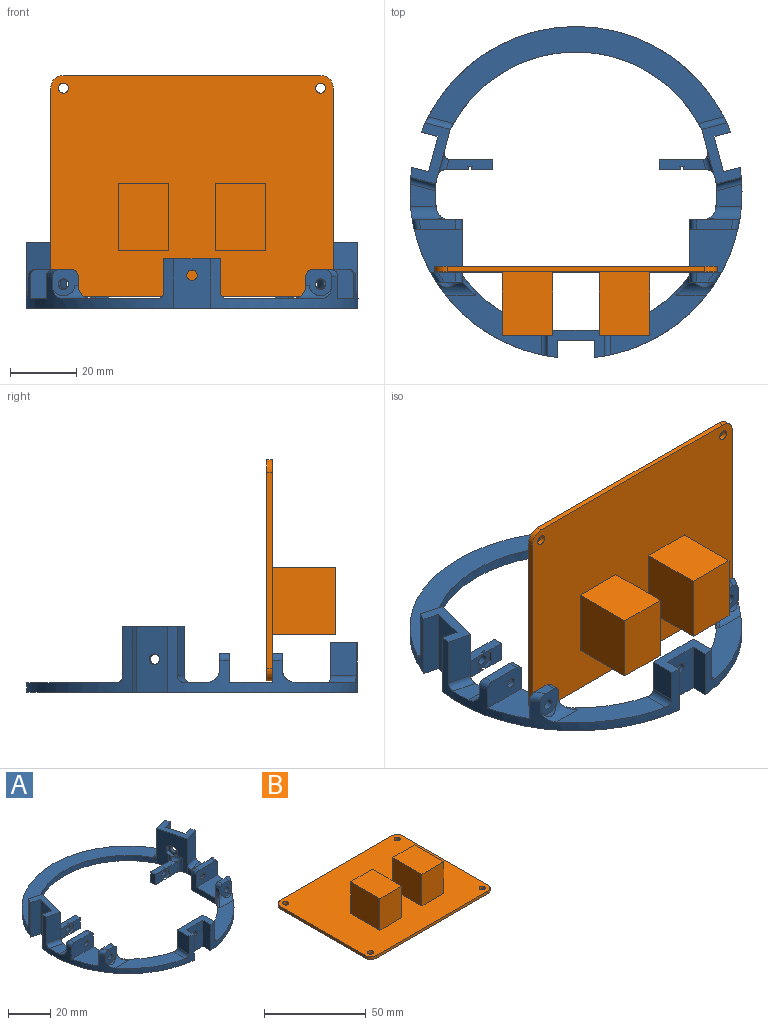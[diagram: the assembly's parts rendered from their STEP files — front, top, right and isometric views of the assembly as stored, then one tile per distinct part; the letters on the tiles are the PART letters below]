
ASSEMBLY  parts=2 mates=1
PART A: 151 faces, bbox 100.8x99.8x20.1 mm
  f0: plane 17x15mm, normal (0,1,0), area 227.6mm2, adj f1,f2,f28,f50,f52,f96,f97,f98
  f1: plane 10x7.77mm, normal (-1,0,0), area 77.7mm2, adj f0,f3,f128,f150
  f2: plane 10x7.77mm, normal (1,0,0), area 77.7mm2, adj f0,f4,f130,f150
  f3: cylinder r=50mm len=57.25mm, axis (0,0,-1), area 383.3mm2, adj f1,f5,f10,f27,f28,f29,f37,f40
  f4: cylinder r=50mm len=57.25mm, axis (0,0,-1), area 383.3mm2, adj f2,f7,f11,f23,f24,f28,f31,f32
  f5: plane 15x5.2mm, normal (1,0,0), area 77.9mm2, adj f3,f6,f28,f150
  f6: plane 15x11mm, normal (0,-1,0), area 157mm2, adj f5,f7,f22,f28,f150
  f7: plane 15x5.2mm, normal (-1,0,0), area 77.9mm2, adj f4,f6,f28,f150
  f8: cylinder r=1.6mm len=3.2mm, axis (0,1,0), area 30.2mm2, adj f54,f57
  f9: cylinder r=1.6mm len=3.2mm, axis (0,1,0), area 30.2mm2, adj f49,f61
  f10: cylinder r=4mm len=11.73mm, axis (1,0,0), area 33mm2, adj f3,f51,f61,f78,f149
  f11: cylinder r=4mm len=11.73mm, axis (1,0,0), area 33mm2, adj f4,f53,f54,f79,f148
  f12: plane 6.57x6mm, normal (0,-1,0), area 28.4mm2, adj f13,f28,f117,f135,f136,f137
  f13: plane 14.07x3.07mm, normal (0,0,1), area 40.2mm2, adj f12,f117,f118,f119,f125,f126,f137,f138
  f14: plane 7.18x6.07mm, normal (0,-1,0), area 32mm2, adj f16,f28,f123,f124,f141,f142,f143
  f15: plane 6.57x6mm, normal (0,-1,0), area 28.4mm2, adj f16,f28,f121,f144,f145,f146
  f16: plane 14.07x3.07mm, normal (0,0,1), area 40.2mm2, adj f14,f15,f120,f121,f122,f123,f143,f144
  f17: cylinder r=1.6mm len=3.2mm, axis (0,-1,0), area 20.1mm2, adj f120,f147
  f18: cylinder r=1.6mm len=3.2mm, axis (0,-1,0), area 20.1mm2, adj f118,f140
  f19: plane 20x16.42mm, normal (0.97,-0.26,0), area 257.2mm2, adj f26,f28,f29,f34,f36,f40,f103,f104
  f20: cylinder r=1.6mm len=3.48mm, axis (-0.97,-0.26,0), area 15.1mm2, adj f45,f116
  f21: cylinder r=1.6mm len=3.48mm, axis (0.97,-0.26,0), area 15.1mm2, adj f39,f109
  f22: cylinder r=1.6mm len=3.2mm, axis (0,1,0), area 15.1mm2, adj f6,f102
  f23: plane 15.18x11.9mm, normal (0,1,0), area 76.9mm2, adj f4,f24,f25,f28,f55,f60,f74,f75
  f24: cylinder r=4mm len=9.61mm, axis (-1,0,0), area 51.3mm2, adj f4,f23,f25,f30,f31,f89,f94
  f25: cylinder r=4mm len=4.92mm, axis (0,0,-1), area 23.3mm2, adj f23,f24,f28,f30,f89,f90
  f26: cylinder r=42.36mm len=7.17mm, axis (0,0,-1), area 22.4mm2, adj f19,f27,f28,f80,f81,f131
  f27: plane 7.85x6.71mm, normal (0,0,1), area 43.6mm2, adj f3,f26,f80,f131
  f28: plane 100x99.7mm, normal (0,0,-1), area 2314.5mm2, adj f0,f3,f4,f5,f6,f7,f12,f14
  f29: plane 15x7.51mm, normal (-0.26,-0.97,0), area 116.6mm2, adj f3,f19,f40,f131
  f30: cylinder r=42.36mm len=7.17mm, axis (0,0,-1), area 22.4mm2, adj f24,f25,f28,f31,f43,f129
  f31: plane 7.85x6.71mm, normal (0,0,1), area 43.6mm2, adj f4,f24,f30,f129
  f32: plane 15x7.51mm, normal (0.26,-0.97,0), area 116.6mm2, adj f4,f43,f46,f129
  f33: cylinder r=50mm len=93.16mm, axis (0,0,-1), area 464.4mm2, adj f28,f35,f36,f38,f40,f41,f42,f46
  f34: cylinder r=42.36mm len=75.77mm, axis (0,0,-1), area 283.1mm2, adj f19,f28,f35,f43,f132,f133
  f35: plane 89x29.24mm, normal (0,0,1), area 761.7mm2, adj f33,f34,f132,f133
  f36: plane 15x7.51mm, normal (0.26,0.97,0), area 116.6mm2, adj f19,f33,f40,f132
  f37: plane 20x5.02mm, normal (0.26,0.97,0), area 103.9mm2, adj f3,f28,f39,f40
  f38: plane 20x5.02mm, normal (-0.26,-0.97,0), area 103.9mm2, adj f28,f33,f39,f40
  f39: plane 20x10.63mm, normal (-0.97,0.26,0), area 212mm2, adj f21,f28,f37,f38,f40
  f40: plane 18.43x11.91mm, normal (0,0,1), area 81mm2, adj f3,f19,f29,f33,f36,f37,f38,f39
  f41: plane 15x7.51mm, normal (-0.26,0.97,0), area 116.6mm2, adj f33,f43,f46,f133
  f42: plane 20x5.02mm, normal (0.26,-0.97,0), area 103.9mm2, adj f28,f33,f45,f46
  f43: plane 20x16.42mm, normal (-0.97,-0.26,0), area 257.2mm2, adj f28,f30,f32,f34,f41,f46,f110,f111
  f44: plane 20x5.02mm, normal (-0.26,0.97,0), area 103.9mm2, adj f4,f28,f45,f46
  f45: plane 20x10.63mm, normal (0.97,0.26,0), area 212mm2, adj f20,f28,f42,f44,f46
  f46: plane 18.43x11.91mm, normal (0,0,1), area 81mm2, adj f4,f32,f33,f41,f42,f43,f44,f45
  f47: plane 18.8x9.76mm, normal (1,0,0), area 77.4mm2, adj f28,f48,f49,f61,f63,f64,f69,f70
  f48: plane 14.44x12.8mm, normal (0,0,1), area 158mm2, adj f3,f47,f49,f63
  f49: plane 9.57x8.76mm, normal (0,1,0), area 73.9mm2, adj f3,f9,f47,f48,f62,f68,f69
  f50: cylinder r=42.36mm len=25.39mm, axis (0,0,-1), area 96.7mm2, adj f0,f28,f51,f76,f78,f128
  f51: plane 28.73x19.27mm, normal (0,0,1), area 214.2mm2, adj f3,f10,f50,f78,f128
  f52: cylinder r=42.36mm len=25.39mm, axis (0,0,-1), area 96.7mm2, adj f0,f28,f53,f77,f79,f130
  f53: plane 28.73x19.27mm, normal (0,0,1), area 214.2mm2, adj f4,f11,f52,f79,f130
  f54: plane 7.95x7.79mm, normal (0,-1,0), area 44.2mm2, adj f4,f8,f11,f55,f58,f72,f73,f148
  f55: plane 18.8x9.76mm, normal (-1,0,0), area 77.4mm2, adj f23,f28,f54,f56,f57,f59,f72,f74
  f56: plane 14.44x12.8mm, normal (0,0,1), area 158mm2, adj f4,f55,f57,f59
  f57: plane 9.57x8.76mm, normal (0,1,0), area 73.9mm2, adj f4,f8,f55,f56,f58,f72,f73
  f58: plane 5.28x3mm, normal (0,0,1), area 13.1mm2, adj f54,f57,f72,f73
  f59: plane 14.44x8.76mm, normal (0,-1,0), area 116.6mm2, adj f4,f55,f56,f60,f67,f74,f75
  f60: plane 11x3mm, normal (0,0,1), area 32.1mm2, adj f23,f59,f74,f75
  f61: plane 7.95x7.79mm, normal (0,-1,0), area 44.1mm2, adj f3,f9,f10,f47,f62,f68,f69,f149
  f62: plane 5.28x3mm, normal (0,0,1), area 13.1mm2, adj f49,f61,f68,f69
  f63: plane 14.44x8.76mm, normal (0,-1,0), area 116.6mm2, adj f3,f47,f48,f65,f66,f70,f71
  f64: plane 15.18x11.9mm, normal (0,1,0), area 76.9mm2, adj f3,f28,f47,f65,f70,f71,f80,f81
  f65: plane 11x3mm, normal (0,0,1), area 32.1mm2, adj f63,f64,f70,f71
  f66: cylinder r=1.6mm len=3.2mm, axis (0,1,0), area 15.1mm2, adj f63,f88
  f67: cylinder r=1.6mm len=3.2mm, axis (0,1,0), area 15.1mm2, adj f59,f95
  f68: torus R=48mm, axis (0,0,1), area 11mm2, adj f3,f49,f61,f62
  f69: cylinder r=2mm len=3mm, axis (0,-1,0), area 9.4mm2, adj f47,f49,f61,f62
  f70: cylinder r=2mm len=3mm, axis (0,-1,0), area 9.4mm2, adj f47,f63,f64,f65
  f71: torus R=48mm, axis (0,0,1), area 9.5mm2, adj f3,f63,f64,f65
  f72: cylinder r=2mm len=3mm, axis (0,1,0), area 9.4mm2, adj f54,f55,f57,f58
  f73: torus R=48mm, axis (0,0,1), area 11mm2, adj f4,f54,f57,f58
  f74: cylinder r=2mm len=3mm, axis (0,1,0), area 9.4mm2, adj f23,f55,f59,f60
  f75: torus R=48mm, axis (0,0,1), area 9.5mm2, adj f4,f23,f59,f60
  f76: cylinder r=2mm len=7mm, axis (0,0,-1), area 7.9mm2, adj f28,f47,f50,f78
  f77: cylinder r=2mm len=7mm, axis (0,0,-1), area 7.9mm2, adj f28,f52,f55,f79
  f78: cylinder r=4mm len=6.78mm, axis (0,1,0), area 11.5mm2, adj f10,f47,f50,f51,f76
  f79: cylinder r=4mm len=6.78mm, axis (0,-1,0), area 11.5mm2, adj f11,f52,f53,f55,f77
  f80: cylinder r=4mm len=9.61mm, axis (-1,0,0), area 51.3mm2, adj f3,f26,f27,f64,f81,f85,f87
  f81: cylinder r=4mm len=4.92mm, axis (0,0,-1), area 23.3mm2, adj f26,f28,f64,f80,f86,f87
  f82: plane 2.81x1.63mm, normal (-0.5,0,-0.87), area 4.9mm2, adj f64,f83,f84,f88
  f83: plane 3.25x1.5mm, normal (-1,0,0), area 4.9mm2, adj f64,f82,f86,f88
  f84: plane 2.81x1.63mm, normal (0.5,0,-0.87), area 4.9mm2, adj f64,f82,f85,f88
  f85: plane 3.25x1.72mm, normal (1,0,0), area 5mm2, adj f64,f80,f84,f87,f88
  f86: plane 2.82x1.63mm, normal (-0.5,0,0.87), area 4.9mm2, adj f64,f81,f83,f87,f88
  f87: plane 2.85x2.12mm, normal (0.5,0,0.87), area 5.9mm2, adj f80,f81,f85,f86,f88
  f88: plane 6.5x5.63mm, normal (0,1,0), area 19.4mm2, adj f66,f82,f83,f84,f85,f86,f87
  f89: plane 2.85x2.12mm, normal (-0.5,0,0.87), area 5.9mm2, adj f24,f25,f90,f94,f95
  f90: plane 2.82x1.63mm, normal (0.5,0,0.87), area 4.9mm2, adj f23,f25,f89,f91,f95
  f91: plane 3.25x1.5mm, normal (1,0,0), area 4.9mm2, adj f23,f90,f92,f95
  f92: plane 2.81x1.63mm, normal (0.5,0,-0.87), area 4.9mm2, adj f23,f91,f93,f95
  f93: plane 2.81x1.63mm, normal (-0.5,0,-0.87), area 4.9mm2, adj f23,f92,f94,f95
  f94: plane 3.25x1.72mm, normal (-1,0,0), area 5mm2, adj f23,f24,f89,f93,f95
  f95: plane 6.5x5.63mm, normal (0,1,0), area 19.4mm2, adj f67,f89,f90,f91,f92,f93,f94
  f96: plane 2.81x1.63mm, normal (0.5,0,-0.87), area 4.9mm2, adj f0,f97,f101,f102
  f97: plane 2.81x1.63mm, normal (-0.5,0,-0.87), area 4.9mm2, adj f0,f96,f98,f102
  f98: plane 3.25x1.5mm, normal (-1,0,0), area 4.9mm2, adj f0,f97,f99,f102
  f99: plane 2.81x1.63mm, normal (-0.5,0,0.87), area 4.9mm2, adj f0,f98,f100,f102
  f100: plane 2.81x1.63mm, normal (0.5,0,0.87), area 4.9mm2, adj f0,f99,f101,f102
  f101: plane 3.25x1.5mm, normal (1,0,0), area 4.9mm2, adj f0,f96,f100,f102
  f102: plane 6.5x5.63mm, normal (0,1,0), area 19.4mm2, adj f22,f96,f97,f98,f99,f100,f101
  f103: plane 3.24x2.73mm, normal (0.13,0.48,0.87), area 5.2mm2, adj f19,f104,f108,f109,f126
  f104: plane 3.26x2.22mm, normal (-0.13,-0.48,0.87), area 5.2mm2, adj f19,f103,f105,f109,f125,f126
  f105: plane 3.25x1.45mm, normal (-0.26,-0.97,0), area 4.9mm2, adj f19,f104,f106,f109
  f106: plane 3.11x2.18mm, normal (-0.13,-0.48,-0.87), area 4.9mm2, adj f19,f105,f107,f109
  f107: plane 3.11x2.18mm, normal (0.13,0.48,-0.87), area 4.9mm2, adj f19,f106,f108,f109
  f108: plane 3.25x1.45mm, normal (0.26,0.97,0), area 4.9mm2, adj f19,f103,f107,f109
  f109: plane 6.5x5.44mm, normal (0.97,-0.26,0), area 19.4mm2, adj f21,f103,f104,f105,f106,f107,f108
  f110: plane 3.24x2.73mm, normal (-0.13,0.48,0.87), area 5.2mm2, adj f43,f111,f115,f116,f123
  f111: plane 3.25x1.45mm, normal (-0.26,0.97,0), area 4.9mm2, adj f43,f110,f112,f116
  f112: plane 3.11x2.18mm, normal (-0.13,0.48,-0.87), area 4.9mm2, adj f43,f111,f113,f116
  f113: plane 3.11x2.18mm, normal (0.13,-0.48,-0.87), area 4.9mm2, adj f43,f112,f114,f116
  f114: plane 3.25x1.45mm, normal (0.26,-0.97,0), area 4.9mm2, adj f43,f113,f115,f116
  f115: plane 3.26x2.22mm, normal (0.13,-0.48,0.87), area 5.2mm2, adj f43,f110,f114,f116,f122,f123
  f116: plane 6.5x5.44mm, normal (-0.97,-0.26,0), area 19.4mm2, adj f20,f110,f111,f112,f113,f114,f115
  f117: plane 6x3mm, normal (1,0,0), area 18mm2, adj f12,f13,f28,f118
  f118: plane 12.73x6mm, normal (0,1,0), area 68.3mm2, adj f13,f18,f28,f117,f125
  f119: plane 7.18x6.07mm, normal (0,-1,0), area 32mm2, adj f13,f28,f126,f127,f134,f138,f139
  f120: plane 12.73x6mm, normal (0,1,0), area 68.3mm2, adj f16,f17,f28,f121,f122
  f121: plane 6x3mm, normal (-1,0,0), area 18mm2, adj f15,f16,f28,f120
  f122: cylinder r=2mm len=7.69mm, axis (0,0,-1), area 24.2mm2, adj f16,f28,f43,f115,f120,f123
  f123: cylinder r=2mm len=6.81mm, axis (0.26,-0.97,0), area 12.1mm2, adj f14,f16,f43,f110,f115,f122,f124
  f124: cylinder r=2mm len=8mm, axis (0,0,-1), area 18mm2, adj f14,f28,f43,f123
  f125: cylinder r=2mm len=7.69mm, axis (0,0,1), area 24.2mm2, adj f13,f19,f28,f104,f118,f126
  f126: cylinder r=2mm len=6.81mm, axis (0.26,0.97,0), area 12.1mm2, adj f13,f19,f103,f104,f119,f125,f127
  f127: cylinder r=2mm len=8mm, axis (0,0,1), area 18mm2, adj f19,f28,f119,f126
  f128: cylinder r=2mm len=8.23mm, axis (0,-1,0), area 24.3mm2, adj f1,f3,f50,f51
  f129: cylinder r=2mm len=8.47mm, axis (0.97,0.26,0), area 24.3mm2, adj f4,f30,f31,f32
  f130: cylinder r=2mm len=8.23mm, axis (0,1,0), area 24.3mm2, adj f2,f4,f52,f53
  f131: cylinder r=2mm len=8.47mm, axis (0.97,-0.26,0), area 24.3mm2, adj f3,f26,f27,f29
  f132: cylinder r=2mm len=8.47mm, axis (-0.97,0.26,0), area 24.3mm2, adj f33,f34,f35,f36
  f133: cylinder r=2mm len=8.47mm, axis (-0.97,-0.26,0), area 24.3mm2, adj f33,f34,f35,f41
  f134: plane 2.38x1.38mm, normal (0.5,0,0.87), area 2.8mm2, adj f28,f119,f139,f140
  f135: plane 2.38x1.38mm, normal (-0.5,0,0.87), area 2.8mm2, adj f12,f28,f136,f140
  f136: plane 3.25x1mm, normal (-1,0,0), area 3.3mm2, adj f12,f135,f137,f140
  f137: plane 2.38x1.38mm, normal (-0.5,0,-0.87), area 2.8mm2, adj f12,f13,f136,f140
  f138: plane 2.38x1.38mm, normal (0.5,0,-0.87), area 2.8mm2, adj f13,f119,f139,f140
  f139: plane 3.25x1mm, normal (1,0,0), area 3.3mm2, adj f119,f134,f138,f140
  f140: plane 6x5.63mm, normal (0,-1,0), area 19.2mm2, adj f13,f18,f28,f134,f135,f136,f137,f138
  f141: plane 2.38x1.38mm, normal (-0.5,0,0.87), area 2.8mm2, adj f14,f28,f142,f147
  f142: plane 3.25x1mm, normal (-1,0,0), area 3.3mm2, adj f14,f141,f143,f147
  f143: plane 2.38x1.38mm, normal (-0.5,0,-0.87), area 2.8mm2, adj f14,f16,f142,f147
  f144: plane 2.38x1.38mm, normal (0.5,0,-0.87), area 2.8mm2, adj f15,f16,f145,f147
  f145: plane 3.25x1mm, normal (1,0,0), area 3.3mm2, adj f15,f144,f146,f147
  f146: plane 2.38x1.38mm, normal (0.5,0,0.87), area 2.8mm2, adj f15,f28,f145,f147
  f147: plane 6x5.63mm, normal (0,-1,0), area 19.2mm2, adj f16,f17,f28,f141,f142,f143,f144,f145
  f148: cylinder r=3.5mm len=6.83mm, axis (0,1,0), area 7.8mm2, adj f4,f11,f54
  f149: cylinder r=3.5mm len=6.83mm, axis (0,1,0), area 7.8mm2, adj f3,f10,f61
  f150: plane 17x8.2mm, normal (0,0,1), area 81mm2, adj f0,f1,f2,f3,f4,f5,f6,f7
PART B: 24 faces, bbox 85.1x66.7x20.6 mm
  f0: plane 85.09x66.68mm, normal (0,0,1), area 5013.3mm2, adj f1,f2,f3,f4,f5,f6,f7,f8
  f1: plane 59.06x1.6mm, normal (1,0,0), area 94.5mm2, adj f0,f2,f12,f13
  f2: cylinder r=3.81mm len=3.81mm, axis (0,0,-1), area 9.6mm2, adj f0,f1,f3,f13
  f3: plane 77.47x1.6mm, normal (0,1,0), area 124mm2, adj f0,f2,f4,f13
  f4: cylinder r=3.81mm len=3.81mm, axis (0,0,-1), area 9.6mm2, adj f0,f3,f5,f13
  f5: plane 59.06x1.6mm, normal (-1,0,0), area 94.5mm2, adj f0,f4,f6,f13
  f6: cylinder r=3.81mm len=3.81mm, axis (0,0,-1), area 9.6mm2, adj f0,f5,f7,f13
  f7: plane 77.47x1.6mm, normal (0,-1,0), area 124mm2, adj f0,f6,f12,f13
  f8: cylinder r=1.5mm len=3mm, axis (0,0,-1), area 15.1mm2, adj f0,f13
  f9: cylinder r=1.5mm len=3mm, axis (0,0,-1), area 15.1mm2, adj f0,f13
  f10: cylinder r=1.5mm len=3mm, axis (0,0,-1), area 15.1mm2, adj f0,f13
  f11: cylinder r=1.5mm len=3mm, axis (0,0,-1), area 15.1mm2, adj f0,f13
  f12: cylinder r=3.81mm len=3.81mm, axis (0,0,-1), area 9.6mm2, adj f0,f1,f7,f13
  f13: plane 85.09x66.68mm, normal (0,0,-1), area 5632.6mm2, adj f1,f2,f3,f4,f5,f6,f7,f8
  f14: plane 20.32x19mm, normal (-1,0,0), area 386.1mm2, adj f0,f15,f17,f18
  f15: plane 19x15.24mm, normal (0,-1,0), area 289.6mm2, adj f0,f14,f16,f18
  f16: plane 20.32x19mm, normal (1,0,0), area 386.1mm2, adj f0,f15,f17,f18
  f17: plane 19x15.24mm, normal (0,1,0), area 289.6mm2, adj f0,f14,f16,f18
  f18: plane 20.32x15.24mm, normal (0,0,1), area 309.7mm2, adj f14,f15,f16,f17
  f19: plane 20.32x19mm, normal (1,0,0), area 386.1mm2, adj f0,f20,f22,f23
  f20: plane 19x15.24mm, normal (0,1,0), area 289.6mm2, adj f0,f19,f21,f23
  f21: plane 20.32x19mm, normal (-1,0,0), area 386.1mm2, adj f0,f20,f22,f23
  f22: plane 19x15.24mm, normal (0,-1,0), area 289.6mm2, adj f0,f19,f21,f23
  f23: plane 20.32x15.24mm, normal (0,0,1), area 309.7mm2, adj f19,f20,f21,f22
PLACE A t=(-726.56,-294.32,-19.68)mm
PLACE B rot(axis=(1,0,0),90deg) t=(-19.11,-16.72,-16.18)mm
MATE fastened B.f10 <-> A.f8  axis (0,-1,0) through (62.17,-18.32,-12.37)mm
